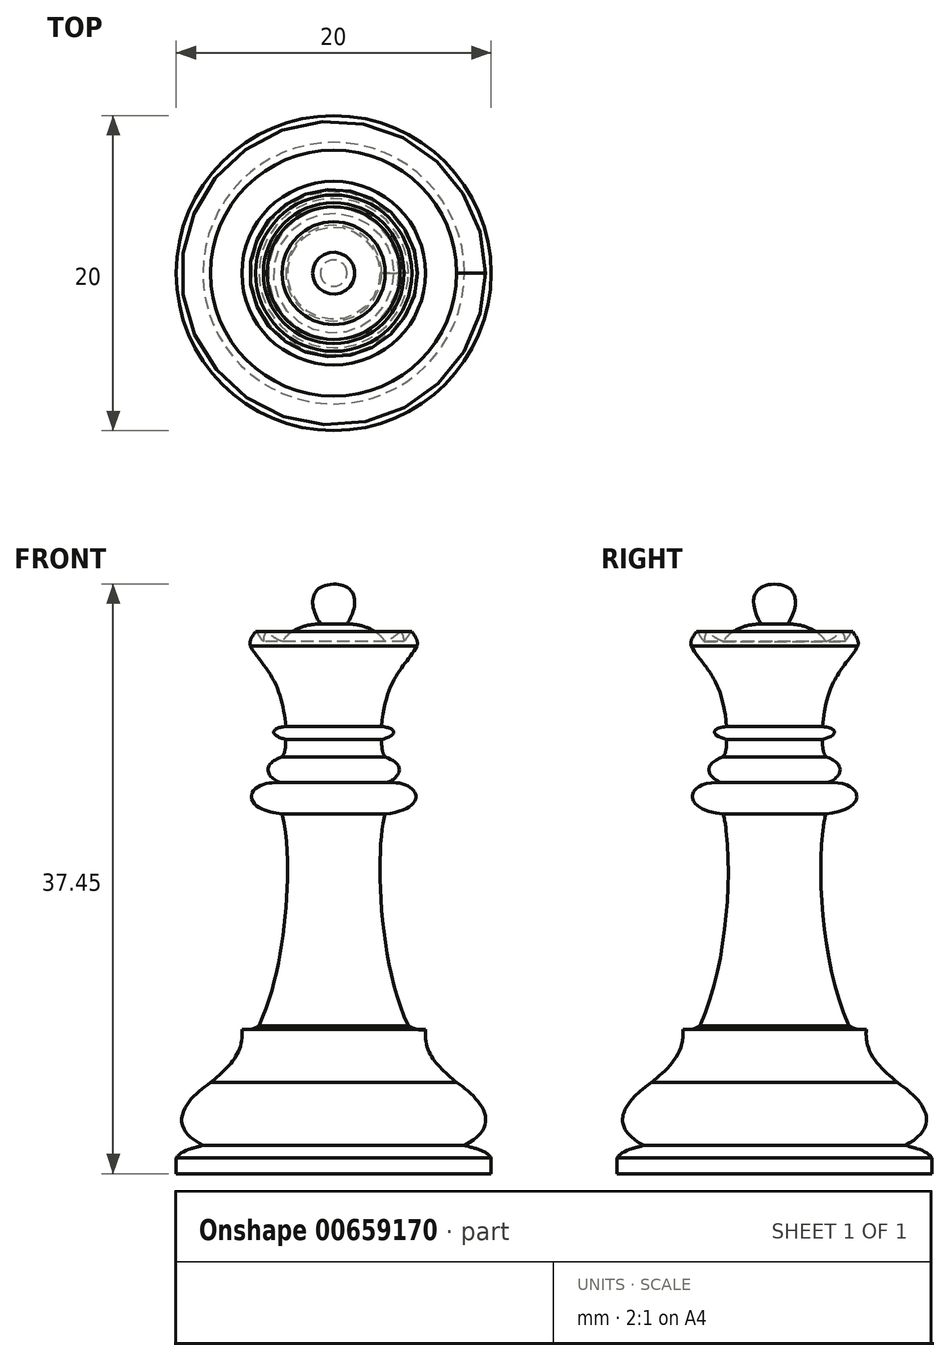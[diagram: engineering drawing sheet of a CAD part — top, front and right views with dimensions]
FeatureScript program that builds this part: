
annotation { "Feature Type Name" : "Feature", "Feature Type Description" : "" }
export const myFeature = defineFeature(function(context is Context, id is Id, definition is map)
    precondition{}
    {
        {
            var Q0;
            Q0=qCreatedBy(makeId("Front.planeOp"),FACE);
            var sketch = newSketch(context, id + "F0", { "sketchPlane" : qUnion([Q0])});
            skLineSegment(sketch, "E0", {"start": v(0, 0) * mm, "end": v(-10, 0) * mm});
            skLineSegment(sketch, "E1", {"start": v(-10, 0) * mm, "end": v(-10, 1) * mm});
            skFitSpline(sketch, "E2", {"points": [v(-10, 1) * mm, v(-8.3, 1.8) * mm], "startDerivative": vector(1.23, 1.65) * mm, "endDerivative": vector(1.89, 0.62) * mm});
            skFitSpline(sketch, "E3", {"points": [v(-8.3, 1.8) * mm, v(-7.82, 5.79) * mm], "startDerivative": vector(-7.85, 4) * mm, "endDerivative": vector(4, 2.71) * mm});
            skFitSpline(sketch, "E4", {"points": [v(-7.82, 5.79) * mm, v(-5.83, 9.16) * mm], "startDerivative": vector(3.3, 2.84) * mm, "endDerivative": vector(-0.4, 4.76) * mm});
            skFitSpline(sketch, "E5", {"points": [v(-5.83, 9.16) * mm, v(-4.74, 9.4) * mm], "startDerivative": vector(1.34, -0.27) * mm, "endDerivative": vector(0.86, 0.54) * mm});
            skFitSpline(sketch, "E6", {"points": [v(-4.74, 9.4) * mm, v(-3.27, 22.85) * mm], "startDerivative": vector(6.17, 13.55) * mm, "endDerivative": vector(-1.7, 5.79) * mm});
            skFitSpline(sketch, "E7", {"points": [v(-3.27, 22.85) * mm, v(-3.27, 24.8) * mm], "startDerivative": vector(-8.77, 0.9) * mm, "endDerivative": vector(6.8, -0.87) * mm});
            skFitSpline(sketch, "E8", {"points": [v(-3.27, 24.8) * mm, v(-3.27, 26.48) * mm], "startDerivative": vector(-1.91, 0.4) * mm, "endDerivative": vector(5, 1.9) * mm});
            skFitSpline(sketch, "E9", {"points": [v(-3.27, 26.48) * mm, v(-3.04, 27.58) * mm], "startDerivative": vector(0.7, 1) * mm, "endDerivative": vector(0.05, 1.16) * mm});
            skFitSpline(sketch, "E10", {"points": [v(-3.04, 27.58) * mm, v(-3.04, 28.4) * mm], "startDerivative": vector(-3.48, 0.96) * mm, "endDerivative": vector(2.67, 0.27) * mm});
            skFitSpline(sketch, "E11", {"points": [v(-3.04, 28.4) * mm, v(-5.3, 33.52) * mm], "startDerivative": vector(-0.86, 9.65) * mm, "endDerivative": vector(-2.19, 3.94) * mm});
            skFitSpline(sketch, "E12", {"points": [v(-5.3, 33.52) * mm, v(-4.97, 34.42) * mm], "startDerivative": vector(-0.24, 1.08) * mm, "endDerivative": vector(0.74, 1.05) * mm});
            skFitSpline(sketch, "E13", {"points": [v(-4.97, 34.42) * mm, v(-4.47, 33.8) * mm], "startDerivative": vector(0.73, -0.54) * mm, "endDerivative": vector(0.52, -0.5) * mm});
            skFitSpline(sketch, "E14", {"points": [v(-4.47, 33.8) * mm, v(-4.22, 34.42) * mm], "startDerivative": vector(0.03, 0.9) * mm, "endDerivative": vector(0.52, 0.27) * mm});
            skFitSpline(sketch, "E15", {"points": [v(-4.22, 34.42) * mm, v(-3.27, 33.8) * mm], "startDerivative": vector(1.06, -0.92) * mm, "endDerivative": vector(1.07, -0.32) * mm});
            skFitSpline(sketch, "E16", {"points": [v(-3.27, 33.8) * mm, v(-0.84, 34.92) * mm], "startDerivative": vector(1.54, 2.27) * mm, "endDerivative": vector(3.01, 0.04) * mm});
            skFitSpline(sketch, "E17", {"points": [v(-0.84, 34.92) * mm, v(0, 37.45) * mm], "startDerivative": vector(-2.24, 3.32) * mm, "endDerivative": vector(4.86, 0.18) * mm});
            skLineSegment(sketch, "E18", {"start": v(0, 37.45) * mm, "end": v(0, 0) * mm});
            skSolve(sketch);
        }
        {
            var Q0;
            Q0 = qSketchRegion(id + "F0", true);
            var Q1;
            Q1=sQuery(id+"F0.wireOp",EDGE,"E18");
            revolve(context, id + "F1", {"entities" : qUnion([Q0]), "axis" : qUnion([Q1]), "revolveType" : RevolveType.FULL});
        }
    });
